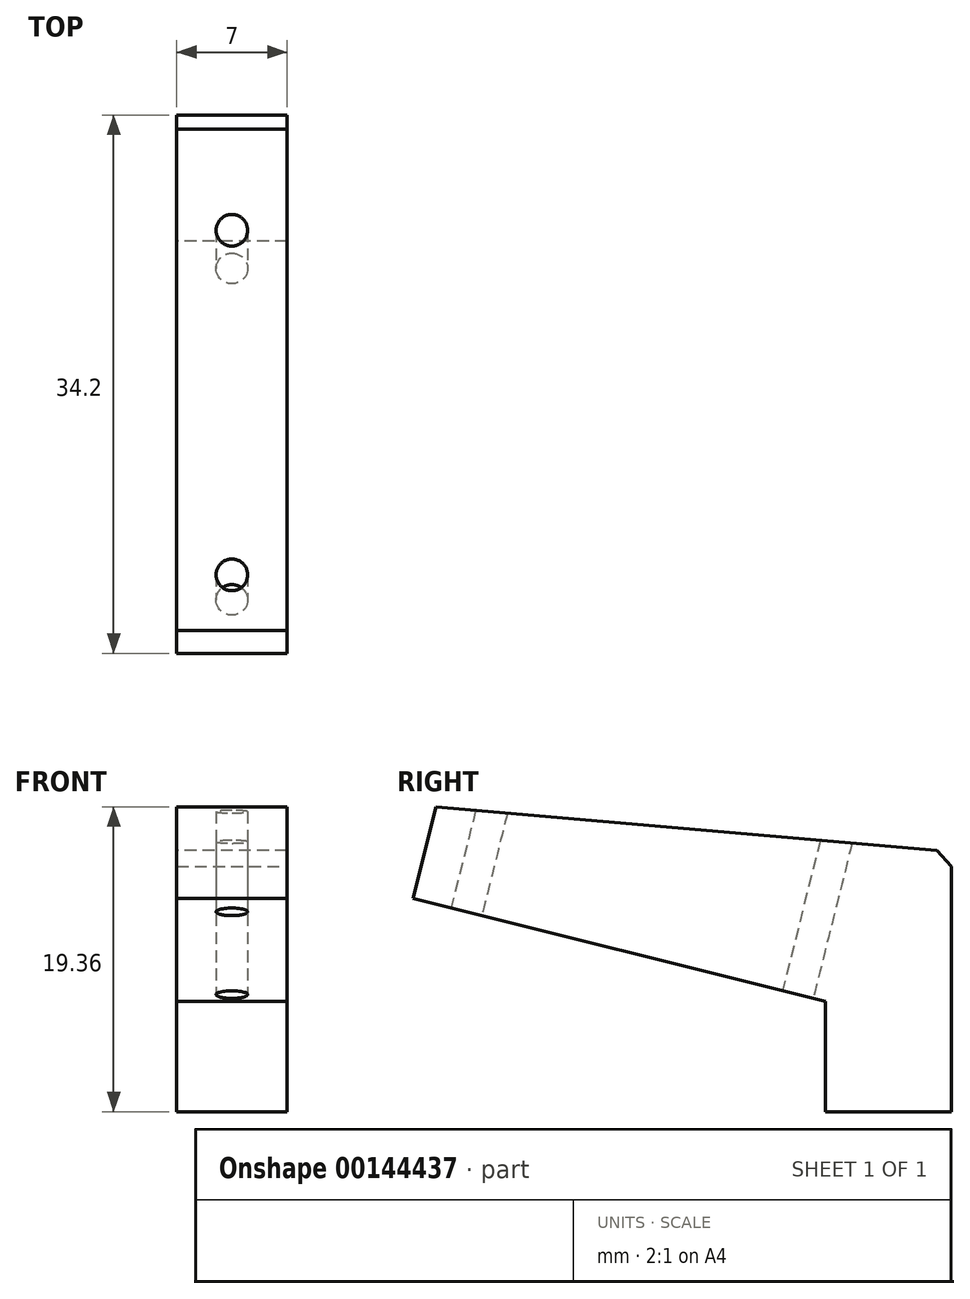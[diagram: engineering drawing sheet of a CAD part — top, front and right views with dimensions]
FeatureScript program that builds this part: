
annotation { "Feature Type Name" : "Feature", "Feature Type Description" : "" }
export const myFeature = defineFeature(function(context is Context, id is Id, definition is map)
    precondition{}
    {
        {
            var Q0;
            Q0=qCreatedBy(makeId("Right.planeOp"),FACE);
            var sketch = newSketch(context, id + "F0", { "sketchPlane" : qUnion([Q0])});
            skLineSegment(sketch, "E0", {"start": v(0, 0) * mm, "end": v(0, -7) * mm});
            skLineSegment(sketch, "E1", {"start": v(0, -7) * mm, "end": v(8, -7) * mm});
            skLineSegment(sketch, "E2", {"start": v(8, -7) * mm, "end": v(8, 9.5) * mm});
            skLineSegment(sketch, "E3", {"start": v(8, 9.5) * mm, "end": v(-24.74, 12.36) * mm});
            skLineSegment(sketch, "E4", {"start": v(-24.74, 12.36) * mm, "end": v(-26.2, 6.54) * mm});
            skLineSegment(sketch, "E5", {"start": v(-26.2, 6.54) * mm, "end": v(0, 0) * mm});
            skSolve(sketch);
        }
        {
            var Q0;
            Q0=makeQuery(id+"F0.imprint","IMPRINT",FACE,{"disambiguationData":[TD([[makeQuery(id+"F0.imprint","IMPRINT",EDGE,{"derivedFrom":sQuery(id+"F0.wireOp",EDGE,"E0")}),1.0]])]});
            extrude(context, id + "F1", {"entities" : qUnion([Q0]), "depth" : 7 * mm});
        }
        {
            var Q0;
            Q0=makeQuery(id+"F1.opExtrude","SWEPT_FACE",FACE,{"disambiguationData":[OSD([sQuery(id+"F0.wireOp",EDGE,"E5")])]});
            var sketch = newSketch(context, id + "F2", { "sketchPlane" : qUnion([Q0])});
            skLineSegment(sketch, "E6.0", {"start": v(0, 27) * mm, "end": v(0, 0) * mm, "construction": true});
            skLineSegment(sketch, "E6.1", {"start": v(7, 27) * mm, "end": v(7, 0) * mm, "construction": true});
            skLineSegment(sketch, "E6.2", {"start": v(7, -1.7) * mm, "end": v(0, -1.7) * mm, "construction": true});
            skLineSegment(sketch, "E6.3", {"start": v(7, 27) * mm, "end": v(0, 27) * mm, "construction": true});
            skPoint(sketch, "E7", {"position": v(3.5, 23.5) * mm});
            skPoint(sketch, "E8", {"position": v(3.5, 1.8) * mm});
            skLineSegment(sketch, "E9", {"start": v(3.5, 27) * mm, "end": v(3.5, 0) * mm, "construction": true});
            skSolve(sketch);
        }
        {
            var Q0;
            Q0=sQuery(id+"F2.wireOp",VERTEX,"E8");
            var Q1;
            Q1=sQuery(id+"F2.wireOp",VERTEX,"E7");
            var Q2;
            Q2=makeQuery(id+"F1.opExtrude","SWEPT_BODY",BODY,{"disambiguationData":[OSD([sQuery(id+"F0.wireOp",EDGE,"E0"),sQuery(id+"F0.wireOp",EDGE,"E1"),sQuery(id+"F0.wireOp",EDGE,"E2"),sQuery(id+"F0.wireOp",EDGE,"E3"),sQuery(id+"F0.wireOp",EDGE,"E4"),sQuery(id+"F0.wireOp",EDGE,"E5")])]});
            hole(context, id + "F3", {"style" : HoleStyle.SIMPLE, "endStyle" : HoleEndStyle.THROUGH, "holeDiameter" : 2 * mm, "locations" : qUnion([Q0, Q1]), "scope" : qUnion([Q2]), "isTappedThrough" : true});
        }
        {
            var Q0;
            Q0=makeQuery(id+"F1.opExtrude","SWEPT_EDGE",EDGE,{"disambiguationData":[OSD([sQuery(id+"F0.wireOp",EDGE,"E2"),sQuery(id+"F0.wireOp",EDGE,"E3")])]});
            chamfer(context, id + "F4", {"entities" : qUnion([Q0]), "width" : 1 * mm, "tangentPropagation" : true});
        }
    });
